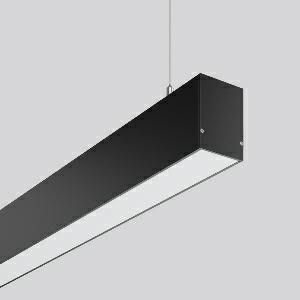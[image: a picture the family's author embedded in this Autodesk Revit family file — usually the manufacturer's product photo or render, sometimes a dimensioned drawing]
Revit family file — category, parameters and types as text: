
# Revit family: less_is_more_50_312311_003_90d2
name_source: partatom
category: Lighting Fixtures
units: mm (PartAtom-declared; Revit-internal decimal feet)

## family parameters
Cut with Voids When Loaded = No
Host = Face
Light Source = No
Part Type = Normal
Room Calculation Point = No
Round Connector Dimension = Use Diameter
Shared = No

## types (1)
- LESS IS MORE 50 (1 x LED Modul 830, 2300 lm, 3000)
    Apparent Load = 22 VA
    CIE Flux Codes = 48 79 95 100 100
    Color Rendering = 80
    Color Temperature = 3000
    Default Elevation = 1800 mm
    Description = Series: LESS IS MORE 50
Linear pendant luminaire for aesthetically sophisticated lighting. Housing: extruded aluminium profile, powder-coated. End cap aluminium powder-coated. Canopy made of aluminium, powder-coated. Diffuser made of non-yellowing plastic (PMMA), opal. Direct light emission. Suitable for pendant. 2-point steel cable suspension freely positionable and infinitely height-adjustable. Special lengths available on request. LED unit with integrated converter interchangeable and removable. Suitable for through-wiring. With sensors or as a safety luminaire on request. 
Colour: deep black, matt (RAL 9005)
Length: 847 mm
Width: 57 mm
Height: 75 mm
Suspension length: 2000 mm
Lamp: LED
Socket: without socket
Colour temperature: 3000K
Colour rendering index (CRI): 80
System power: 22 W
Rated luminous flux: 2300 lm
Luminous efficiency: 105 lm/W
Control gear: Regulated power supply
Protection class: I
Type of protection: IP 20
    Height = 75 mm
    Lamp = 1 x LED Modul 830
    Lamp Light Flux = 2300 lm
    Lamp count = 1
    Length = 847 mm
    Lifetime = 50000 h
    Luminous efficacy = 105 lm/W
    Manufacturer = RZB
    ModVariant = No
    Model = 312311.003
    Mounting Place = Ceiling
    Mounting Type = Pendant
    Number of Poles = 1
    OnlyDefault = Yes
    Power Factor = 1
    Product Name = LESS IS MORE 50
    Product group = Pendant LED linear luminaires
    ProductGroupID = 907
    Protection Class = Protection class I
    Protection Degree = IP 20
    RLX_Detail_Level = 1
    RLX_Emergency_Light_Flux = 0 lm
    RLX_Emergency_Type = 0
    RLX_Emergency_Type_DB = No
    RlxData = <blob elided: 28853 chars, md5=cff7fe13>
    Socket = socket
    Standby Power = 0 W
    System Light Flux = 2300 lm
    System Power = 22 W
    Type Comments = Product without accessories
    Type Image = 312318.003.jpg
    URL = http://relux.com
    VarID = ---
    Voltage = 230 V
    Voltage Range = 220-240 V
    Weight = 0.00 kg
    Width = 57 mm

## geometry (parser evidence)
native form markers: Blend x4, Sweep x10
no freeform markers — native parametric forms only
